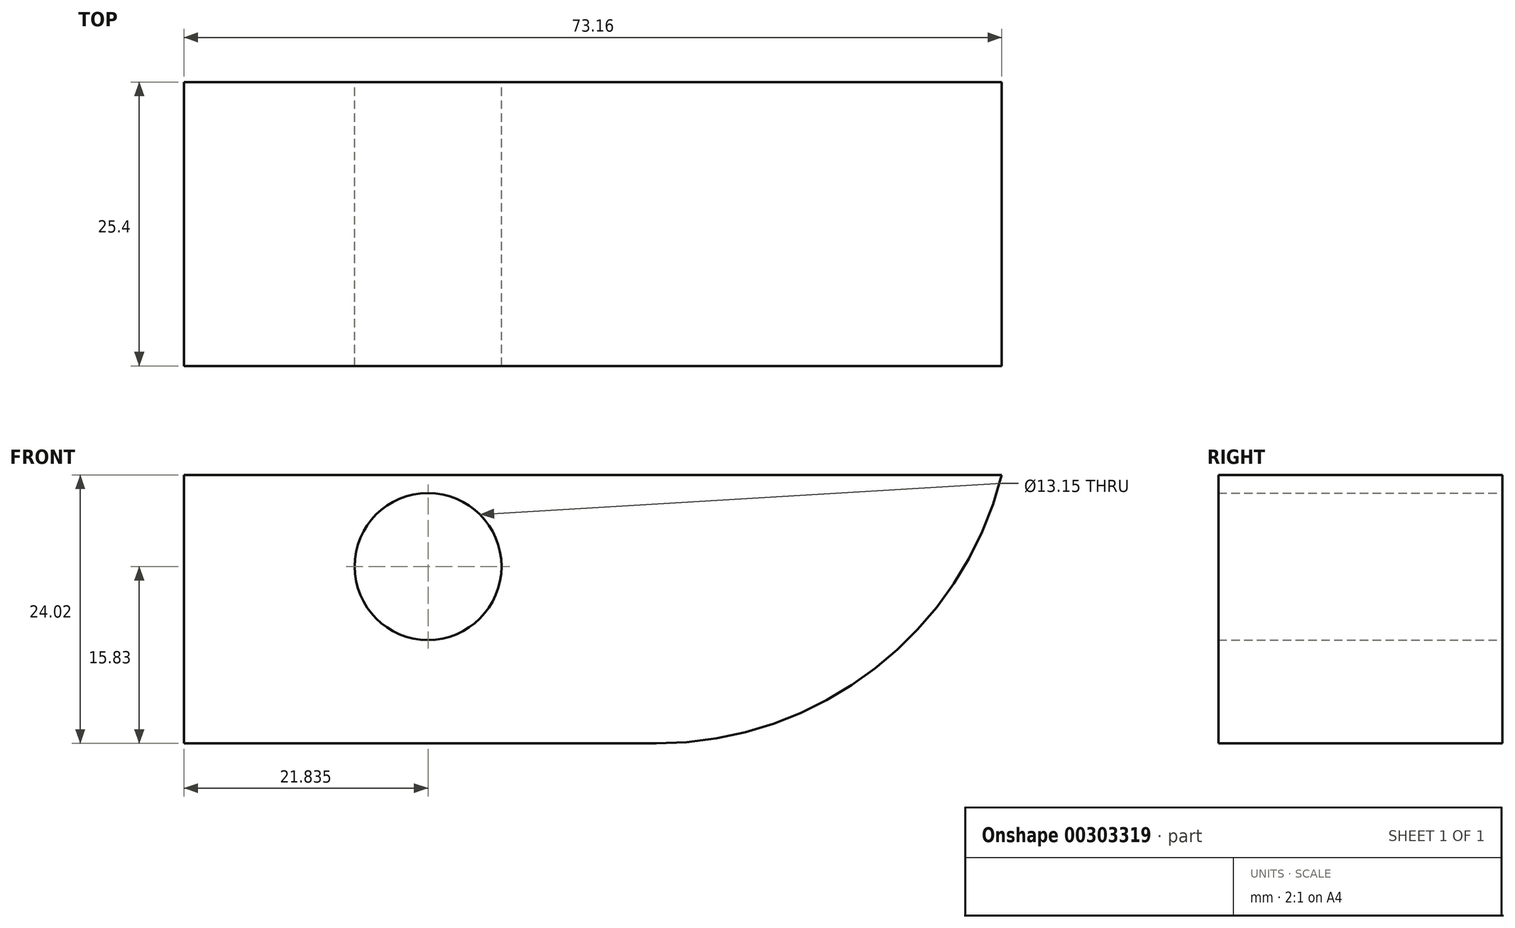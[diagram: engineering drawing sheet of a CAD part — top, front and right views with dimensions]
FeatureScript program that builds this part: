
annotation { "Feature Type Name" : "Feature", "Feature Type Description" : "" }
export const myFeature = defineFeature(function(context is Context, id is Id, definition is map)
    precondition{}
    {
        {
            var Q0;
            Q0=qCreatedBy(makeId("Front.planeOp"),FACE);
            var sketch = newSketch(context, id + "F0", { "sketchPlane" : qUnion([Q0])});
            skLineSegment(sketch, "E0.bottom", {"start": v(-36.85, -15.83) * mm, "end": v(36.3, -15.83) * mm});
            skLineSegment(sketch, "E0.top", {"start": v(-36.85, 8.19) * mm, "end": v(36.3, 8.19) * mm});
            skLineSegment(sketch, "E0.left", {"start": v(-36.85, -15.83) * mm, "end": v(-36.85, 8.19) * mm});
            skLineSegment(sketch, "E0.right", {"start": v(36.3, -15.83) * mm, "end": v(36.3, 8.19) * mm});
            skCircle(sketch, "E1", {"center": v(-15.01, 0) * mm, "radius": 6.57 * mm});
            skSolve(sketch);
        }
        {
            var Q0;
            Q0=makeQuery(id+"F0.imprint","IMPRINT",FACE,{"disambiguationData":[TD([[makeQuery(id+"F0.imprint","IMPRINT",EDGE,{"derivedFrom":sQuery(id+"F0.wireOp",EDGE,"E0.bottom")}),1.0]])]});
            extrude(context, id + "F1", {"entities" : qUnion([Q0]), "depth" : 25.4 * mm});
        }
        {
            var Q0;
            Q0=makeQuery(id+"F1.opExtrude","SWEPT_EDGE",EDGE,{"disambiguationData":[OSD([sQuery(id+"F0.wireOp",EDGE,"E0.bottom"),sQuery(id+"F0.wireOp",EDGE,"E0.right")])]});
            fillet(context, id + "F2", {"entities" : qUnion([Q0]), "radius" : 31.9 * mm, "tangentPropagation" : true, "allowEdgeOverflow" : false});
        }
    });
